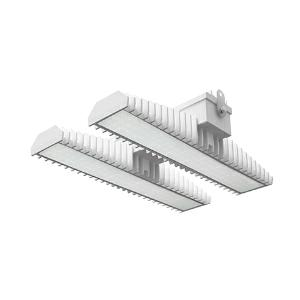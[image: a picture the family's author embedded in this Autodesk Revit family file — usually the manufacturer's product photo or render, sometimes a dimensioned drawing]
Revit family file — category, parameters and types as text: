
# Revit family: 3f_filippi_-_3f_lem_ht_ampio_3f_filippi_-_59026_a0811_-_3f_lem_2_ht_led_60_cr_ampio___vt_53f5
name_source: partatom
category: Lighting Fixtures
units: mm (PartAtom-declared; Revit-internal decimal feet)

## family parameters
Cut with Voids When Loaded = No
Host = Face
Light Source = No
Part Type = Normal
Room Calculation Point = No
Round Connector Dimension = Use Diameter
Shared = No

## types (1)
- 3F Filippi - 3F LEM HT Ampio (1 x LED, 10119 lm, 68 W, 4000 K)
    Apparent Load = 68 VA
    Approval mark = ENEC
    CIE Flux Codes = 60 92 99 100 100
    Color Rendering = 80
    Color Temperature = 4000 K
    Control Gear = Electronic ballast
    Default Elevation = 1800 mm
    Description = Industrial luminaire with high light output and high luminous efficiency designed with the most innovative technologies for environments with temperature up to 70°C.

ILLUMINOTECHNICAL
Luminous efficiency 100% (DLOR 99%, ULOR 1%).
Initial luminous flux of the luminaire 10119 lm.
Direct symmetric wide distribution: the illuminated area has a rectangular shape.
Installation Interdistance Transv.D = 1.58 x hu - Long.D = 1.45 x hu.
Tabular UGR (CIE 117 - 4H-8H; S=0.25H; 70/50/20): RUG 20.6 - 21.6.
Beam angle: 93° - 99°.
Luminous efficacy 149 lm/W.
Lifetime (L93/B10): 30000 h. (tq+25°C)
Lifetime (L90/B10): 50000 h. (tq+25°C)
Lifetime (L85/B10): 80000 h. (tq+25°C)
Lifetime (L80/B10): 100000 h. (tq+25°C)
Lifetime (L85/B10): 50000 h. (tq+70°C)
Sudden decreased luminous flux after 50000 hours: 0% (C0).
Photobiological safety in compliance with IEC/TR 62778: RG0 risk exempt, (IEC 62471).
In compliance with IEC/EN 62722-2-1 - IEC/EN 62717 standards.
Luminous flux at +70°C: -13.5%.

SOURCE
2 Mid-Power linear LED modules 30W/840.
Energy efficiency class (UE 2019/2020 - UE 2019/2015): C.
CIE 13.3 Colour rendering index: CRI >80 (R9 <50%).
IES TM-30 Fidelity Index: Rf = 84 Rg = 95.
CCT nominal colour temperature 4000 K.
Colour initial tolerance (MacAdam): SDCM 3.

MECHANICAL
Passive modular heatsinks in die-casted aluminium, painted in white colour.
To optimize the thermal management of the LED module, the heatsinks are oversized and provided with self-cleaning of cooling fins.
Wiring body in aluminium and galvanised steel anchored solidly to the sinks and thermally separated.
3F Lens lenses with high luminous efficiency, transparent polycarbonate, fixed to the LED modules.
Fixing brackets in stainless steel.
Luminaire with limited surface temperature. - D - (EN 60598-2-24)
Dimensions: 470x542 mm, height 133 mm. Weight 9.989 kg.
IP65 protection degree.
Mechanical strength to impacts IK08 (5 joule).
Glow-wire test resistance 850°C.

ELECTRICAL
Halogen Free electronic wiring 230V-50/60Hz, power factor 0.95, THD <25%, constant output current, class I, 1 driver.
Power of the luminaire 68 W.
CE - IEC 60598-1 - EN 60598-1.
SAFE FLICKER: PstLM=<1 and SVM=<0.4 (IEC TR 61547-1 and IEC TR 63158), to ensure a more comfortable and safe light.
Luminaire compliant with EN 60598-2-22 for power supply from a centralised emergency system CPSS (Central Power Supply System), not incorporated in the luminaire - high risk areas excluded. The default power and flux are 100% in AC and 100% in DC.
Ambient temperature from -30°C to +70°C.
Temperature class T6 max 85°C.
Quick connection via M20 3P connector with 9-13 mm tightening range.
Power unit positioned on a separate compartment by the LED module to ensure optimum temperatures of cabling components, to be inspectable and maintainable.
Relative humidity UR: <85%.

INSTALLATION
Ceiling / Suspended / Wall.
All accessories dedicated to this product are available on the Catalog and on our website www.3F-Filippi.com.

ACCESSORIES
A0811 - VT transparent glass, tempered, not flammable, with sealing gasket.
One required for each light module. The pack contains 10 pieces.

APPLICATIONS
In commercial environments, exhibition and industrial areas, stores, open areas.
Applications with high ambient temperature up to 70°C.

WARNING
Fixture not suitable for cold stores with an ambient temperature <0°C and/or relative humidity >85%.
Luminaire designed for disposal/recycling at end-of-life.
Replaceable (LED only) light source by a professional. Replaceable control gear by a professional.
    Height = 133 mm  [stored 0.436352 ft]
    Lamp = 1 x LED
    Lamp Light Flux = 10119 lm
    Lamp Power = 68 W
    Lamp count = 1
    Length = 470 mm
    Lifetime = 50000 h
    Luminous efficacy = 149 lm/W
    Manufacturer = 3F Filippi
    ModVariant = No
    Model = 3F Filippi - 59026+A0811 - 3F LEM 2 HT LED 60 CR AMPIO + VT
    Mounting Place = Ceiling
    Mounting Type = Pendant
    Number of Poles = 1
    OnlyDefault = Yes
    Power Factor = 1
    Product Name = 3F Filippi - 3F LEM HT Ampio
    Product group = pendant luminaire
    ProductGroupID = 9
    Protection Class = Protection class I
    Protection Degree = IP 65
    RLX_Detail_Level = 1
    RLX_Emergency_Light_Flux = 0 lm
    RLX_Emergency_Type = 0
    RLX_Emergency_Type_DB = No
    RlxData = <blob elided: 94381 chars, md5=c299ff6f>
    Socket = socket
    Standby Power = 0 W
    System Light Flux = 10119 lm
    System Power = 68 W
    Type Comments = Product without accessories
    Type Image = 3f_filippi_-_lem_2__a0812.jpg
    URL = http://relux.com
    VarID = ---
    Voltage = 0 V
    Weight = 0.00 kg
    Width = 542 mm

note: [stored X ft] marks values corroborated as IEEE doubles in the binary element streams (Revit-internal decimal feet)

## geometry (parser evidence)
native form markers: Blend x4, Sweep x10
no freeform markers — native parametric forms only
